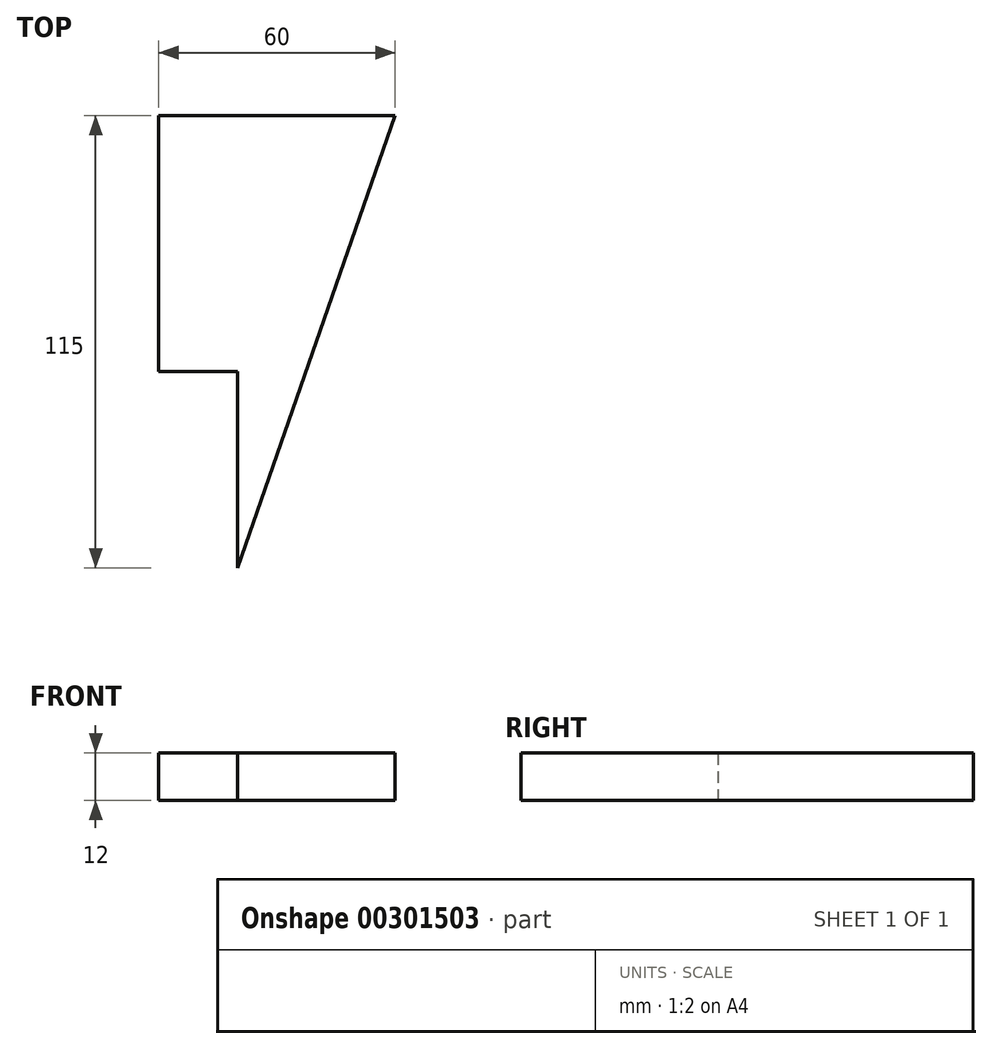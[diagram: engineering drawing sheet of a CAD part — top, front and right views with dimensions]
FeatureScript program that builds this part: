
annotation { "Feature Type Name" : "Feature", "Feature Type Description" : "" }
export const myFeature = defineFeature(function(context is Context, id is Id, definition is map)
    precondition{}
    {
        {
            var Q0;
            Q0=qCreatedBy(makeId("Top.planeOp"),FACE);
            var sketch = newSketch(context, id + "F0", { "sketchPlane" : qUnion([Q0])});
            skLineSegment(sketch, "E0.bottom", {"start": v(0, 0) * mm, "end": v(60, 0) * mm});
            skLineSegment(sketch, "E0.top", {"start": v(0, 115) * mm, "end": v(60, 115) * mm});
            skLineSegment(sketch, "E0.left", {"start": v(0, 0) * mm, "end": v(0, 115) * mm});
            skLineSegment(sketch, "E0.right", {"start": v(60, 0) * mm, "end": v(60, 115) * mm});
            skLineSegment(sketch, "E1", {"start": v(20, 0) * mm, "end": v(60, 115) * mm});
            skLineSegment(sketch, "E2.bottom", {"start": v(0, 0) * mm, "end": v(20, 0) * mm});
            skLineSegment(sketch, "E2.top", {"start": v(0, 50) * mm, "end": v(20, 50) * mm});
            skLineSegment(sketch, "E2.left", {"start": v(0, 0) * mm, "end": v(0, 50) * mm});
            skLineSegment(sketch, "E2.right", {"start": v(20, 0) * mm, "end": v(20, 50) * mm});
            skSolve(sketch);
        }
        {
            var Q0;
            Q0=makeQuery(id+"F0.imprint","IMPRINT",FACE,{"disambiguationData":[TD([[makeQuery(id+"F0.imprint","IMPRINT",EDGE,{"derivedFrom":sQuery(id+"F0.wireOp",EDGE,"E0.top")}),-1.0]])]});
            extrude(context, id + "F1", {"entities" : qUnion([Q0]), "depth" : 12 * mm});
        }
    });
